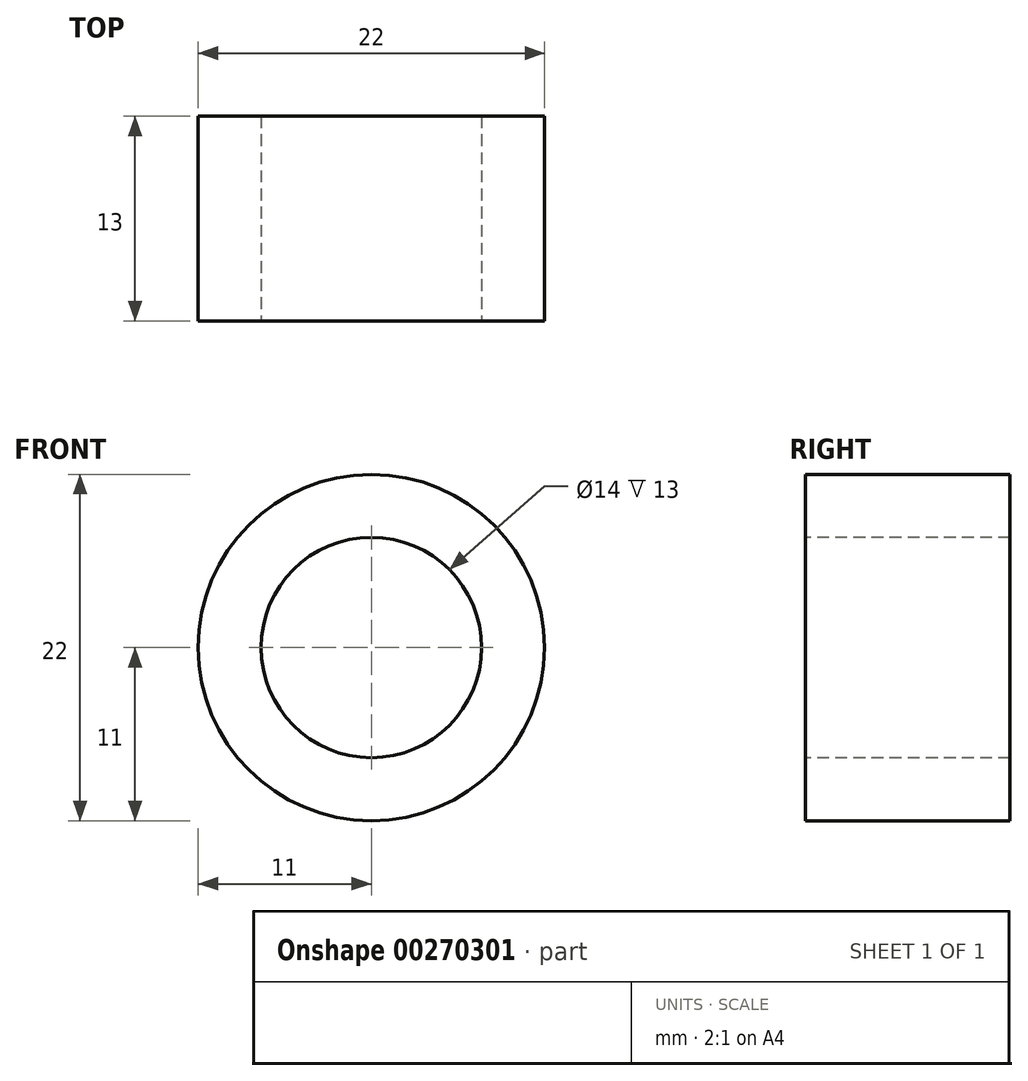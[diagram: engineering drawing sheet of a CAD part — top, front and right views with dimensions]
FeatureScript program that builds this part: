
annotation { "Feature Type Name" : "Feature", "Feature Type Description" : "" }
export const myFeature = defineFeature(function(context is Context, id is Id, definition is map)
    precondition{}
    {
        {
            var Q0;
            Q0=qCreatedBy(makeId("Front.planeOp"),FACE);
            var sketch = newSketch(context, id + "F0", { "sketchPlane" : qUnion([Q0])});
            skCircle(sketch, "E0", {"center": v(0, 0) * mm, "radius": 7 * mm});
            skCircle(sketch, "E1", {"center": v(0, 0) * mm, "radius": 11 * mm});
            skSolve(sketch);
        }
        {
            var Q0;
            Q0=makeQuery(id+"F0.imprint","IMPRINT",FACE,{"disambiguationData":[TD([[makeQuery(id+"F0.imprint","IMPRINT",EDGE,{"derivedFrom":sQuery(id+"F0.wireOp",EDGE,"E0")}),-1.0]])]});
            extrude(context, id + "F1", {"entities" : qUnion([Q0]), "oppositeDirection" : true, "depth" : 13 * mm});
        }
    });
